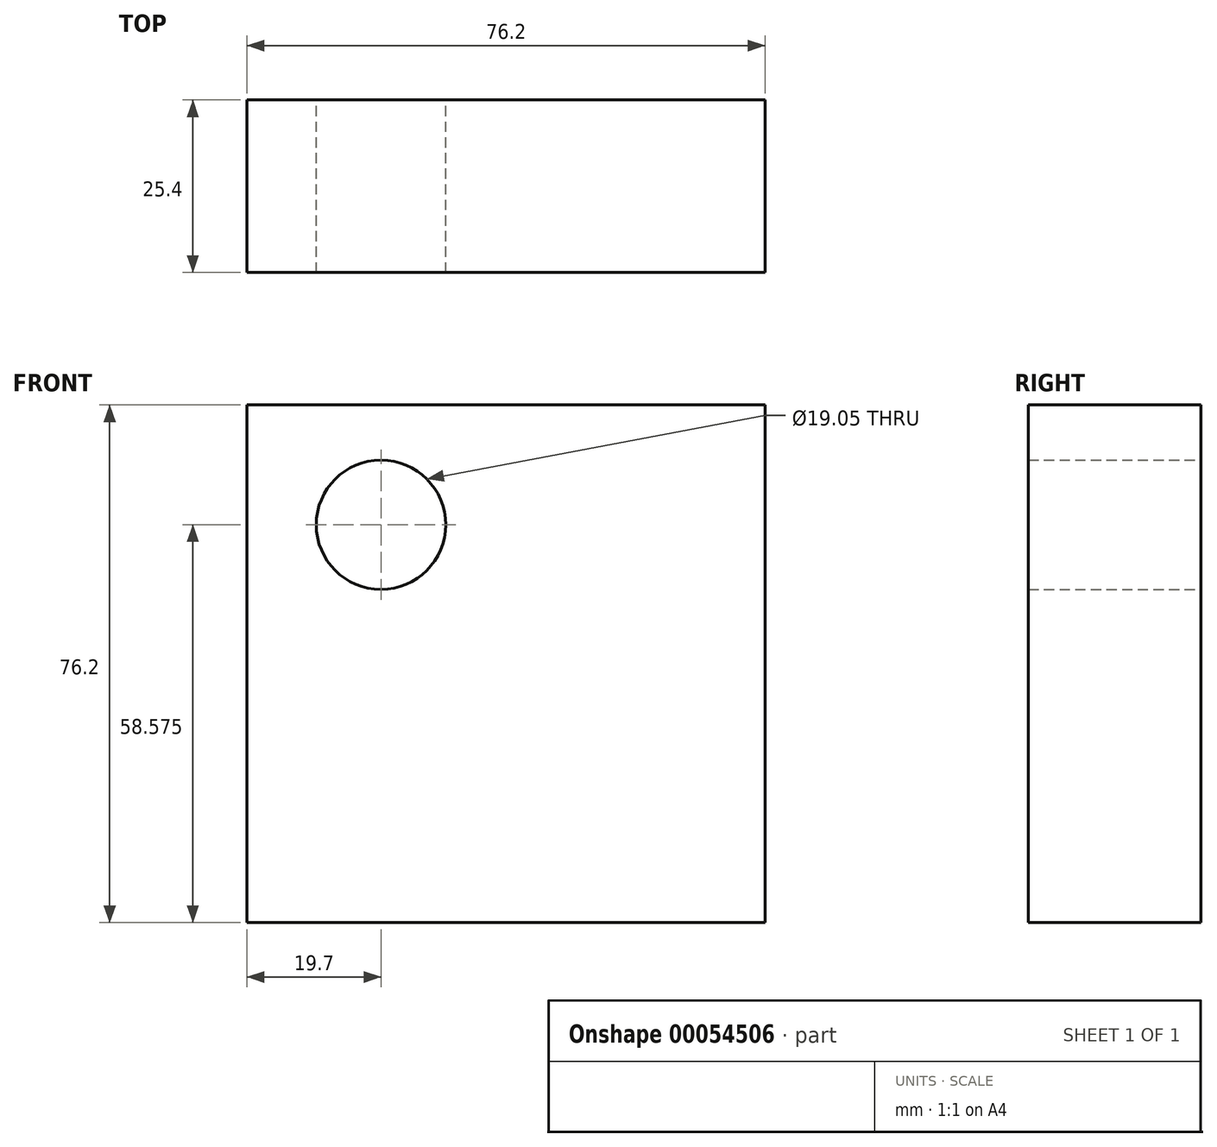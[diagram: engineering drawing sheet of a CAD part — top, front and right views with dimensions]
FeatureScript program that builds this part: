
annotation { "Feature Type Name" : "Feature", "Feature Type Description" : "" }
export const myFeature = defineFeature(function(context is Context, id is Id, definition is map)
    precondition{}
    {
        {
            var Q0;
            Q0=qCreatedBy(makeId("Front.planeOp"),FACE);
            var sketch = newSketch(context, id + "F0", { "sketchPlane" : qUnion([Q0])});
            skLineSegment(sketch, "E0.bottom", {"start": v(-30.02, 54.33) * mm, "end": v(46.18, 54.33) * mm});
            skLineSegment(sketch, "E0.top", {"start": v(-30.02, -21.87) * mm, "end": v(46.18, -21.87) * mm});
            skLineSegment(sketch, "E0.left", {"start": v(-30.02, 54.33) * mm, "end": v(-30.02, -21.87) * mm});
            skLineSegment(sketch, "E0.right", {"start": v(46.18, 54.33) * mm, "end": v(46.18, -21.87) * mm});
            skCircle(sketch, "E1", {"center": v(-10.32, 36.7) * mm, "radius": 9.53 * mm});
            skSolve(sketch);
        }
        {
            var Q0;
            Q0=makeQuery(id+"F0.imprint","IMPRINT",FACE,{"disambiguationData":[TD([[makeQuery(id+"F0.imprint","IMPRINT",EDGE,{"derivedFrom":sQuery(id+"F0.wireOp",EDGE,"E0.bottom")}),-1.0]])]});
            extrude(context, id + "F1", {"entities" : qUnion([Q0]), "depth" : 25.4 * mm});
        }
    });
